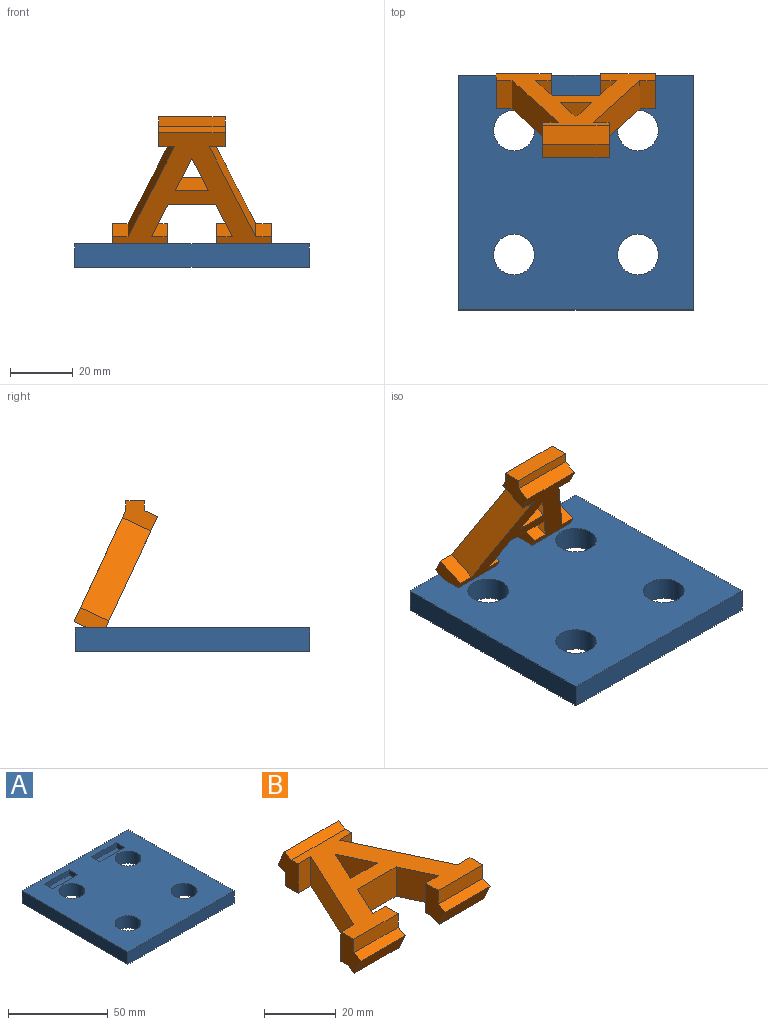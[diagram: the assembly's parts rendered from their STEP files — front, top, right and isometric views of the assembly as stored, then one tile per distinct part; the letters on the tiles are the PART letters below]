
ASSEMBLY  parts=2 mates=1
PART A: 20 faces, bbox 75x75x7.5 mm
  f0: plane 75x75mm, normal (0,0,1), area 4887mm2, adj f1,f2,f3,f4,f6,f7,f8,f9
  f1: plane 75x7.5mm, normal (-1,0,0), area 562.5mm2, adj f0,f2,f4,f5
  f2: plane 75x7.5mm, normal (0,-1,0), area 562.5mm2, adj f0,f1,f3,f5
  f3: plane 75x7.5mm, normal (1,0,0), area 562.5mm2, adj f0,f2,f4,f5
  f4: plane 75x7.5mm, normal (0,1,0), area 562.5mm2, adj f0,f1,f3,f5
  f5: plane 75x75mm, normal (0,0,-1), area 5094.1mm2, adj f1,f2,f3,f4,f6,f7,f8,f9
  f6: cylinder r=6.5mm len=13mm, axis (0,0,-1), area 306.3mm2, adj f0,f5
  f7: cylinder r=6.5mm len=13mm, axis (0,0,-1), area 306.3mm2, adj f0,f5
  f8: cylinder r=6.5mm len=13mm, axis (0,0,-1), area 306.3mm2, adj f0,f5
  f9: cylinder r=6.5mm len=13mm, axis (0,0,-1), area 306.3mm2, adj f0,f5
  f10: plane 17.5x3.18mm, normal (0,-1,0), area 55.6mm2, adj f0,f11,f13,f14
  f11: plane 5.92x3.18mm, normal (1,0,0), area 18.8mm2, adj f0,f10,f12,f14
  f12: plane 17.5x3.18mm, normal (0,1,0), area 55.6mm2, adj f0,f11,f13,f14
  f13: plane 5.92x3.18mm, normal (-1,0,0), area 18.8mm2, adj f0,f10,f12,f14
  f14: plane 17.5x5.92mm, normal (0,0,1), area 103.5mm2, adj f10,f11,f12,f13
  f15: plane 5.92x3.18mm, normal (-1,0,0), area 18.8mm2, adj f0,f16,f18,f19
  f16: plane 17.5x3.18mm, normal (0,-1,0), area 55.6mm2, adj f0,f15,f17,f19
  f17: plane 5.92x3.18mm, normal (1,0,0), area 18.8mm2, adj f0,f16,f18,f19
  f18: plane 17.5x3.18mm, normal (0,1,0), area 55.6mm2, adj f0,f15,f17,f19
  f19: plane 17.5x5.92mm, normal (0,0,1), area 103.5mm2, adj f15,f16,f17,f18
PART B: 34 faces, bbox 50.8x47.5x12.7 mm
  f0: plane 50.79x39.22mm, normal (0,0,1), area 760.6mm2, adj f2,f3,f4,f5,f6,f7,f8,f9
  f1: plane 50.79x39.22mm, normal (0,0,-1), area 726.2mm2, adj f3,f4,f5,f6,f7,f8,f9,f11
  f2: plane 17.5x4.64mm, normal (0,-1,0), area 81.2mm2, adj f0,f3,f21,f31
  f3: plane 11.34x7.88mm, normal (1,0,0), area 62.1mm2, adj f0,f1,f2,f4,f31,f32,f33
  f4: plane 10x5mm, normal (0,1,0), area 50mm2, adj f0,f1,f3,f5
  f5: plane 11.33x10mm, normal (0.91,-0.42,0), area 125mm2, adj f0,f1,f4,f6
  f6: plane 15.23x10mm, normal (0,-1,0), area 152.3mm2, adj f0,f1,f5,f7
  f7: plane 11.33x10mm, normal (-0.91,-0.42,0), area 125mm2, adj f0,f1,f6,f8
  f8: plane 10x5mm, normal (0,1,0), area 50mm2, adj f0,f1,f7,f9
  f9: plane 11.34x7.88mm, normal (-1,0,0), area 62.1mm2, adj f0,f1,f8,f10,f28,f29,f30
  f10: plane 17.5x4.64mm, normal (0,-1,0), area 81.2mm2, adj f0,f9,f11,f29
  f11: plane 11.34x7.88mm, normal (1,0,0), area 62.1mm2, adj f0,f1,f10,f12,f28,f29,f30
  f12: plane 10x5mm, normal (0,1,0), area 50mm2, adj f0,f1,f11,f13
  f13: plane 31.72x14.79mm, normal (0.91,0.42,0), area 350mm2, adj f0,f1,f12,f14
  f14: plane 10x5mm, normal (0,-1,0), area 50mm2, adj f0,f1,f13,f15
  f15: plane 11.34x7.88mm, normal (1,0,0), area 62.1mm2, adj f0,f1,f14,f16,f25,f26,f27
  f16: plane 21.21x4.64mm, normal (0,1,0), area 98.4mm2, adj f1,f15,f17,f26
  f17: plane 11.34x7.88mm, normal (-1,0,0), area 62.1mm2, adj f0,f1,f16,f18,f25,f26,f27
  f18: plane 10x5mm, normal (0,-1,0), area 50mm2, adj f0,f1,f17,f19
  f19: plane 31.72x14.79mm, normal (-0.91,0.42,0), area 350mm2, adj f0,f1,f18,f20
  f20: plane 10x5mm, normal (0,1,0), area 50mm2, adj f0,f1,f19,f21
  f21: plane 11.34x7.88mm, normal (-1,0,0), area 62.1mm2, adj f0,f1,f2,f20,f31,f32,f33
  f22: plane 11.33x10mm, normal (-0.91,-0.42,0), area 125mm2, adj f0,f1,f23,f24
  f23: plane 11.33x10mm, normal (0.91,-0.42,0), area 125mm2, adj f0,f1,f22,f24
  f24: plane 10.57x10mm, normal (0,1,0), area 105.7mm2, adj f0,f1,f22,f23
  f25: plane 21.21x2.88mm, normal (0,-0.42,0.91), area 67.3mm2, adj f0,f15,f17,f27
  f26: plane 21.21x2.88mm, normal (0,0.42,-0.91), area 67.3mm2, adj f15,f16,f17,f27
  f27: plane 21.21x5.36mm, normal (0,0.91,0.42), area 125.5mm2, adj f15,f17,f25,f26
  f28: plane 17.5x2.88mm, normal (0,0.42,-0.91), area 55.6mm2, adj f1,f9,f11,f30
  f29: plane 17.5x2.88mm, normal (0,-0.42,0.91), area 55.6mm2, adj f9,f10,f11,f30
  f30: plane 17.5x5.36mm, normal (0,-0.91,-0.42), area 103.5mm2, adj f9,f11,f28,f29
  f31: plane 17.5x2.88mm, normal (0,-0.42,0.91), area 55.6mm2, adj f2,f3,f21,f33
  f32: plane 17.5x2.88mm, normal (0,0.42,-0.91), area 55.6mm2, adj f1,f3,f21,f33
  f33: plane 17.5x5.36mm, normal (0,-0.91,-0.42), area 103.5mm2, adj f3,f21,f31,f32
PLACE A t=(-0.43,-13.5,0.15)mm fixed
PLACE B rot(axis=(0,0.54,0.84),180deg) t=(62.43,52.83,5.39)mm
MATE fastened A.f19 <-> B.f30  axis (0,0,1) through (20.38,54.74,4.48)mm
